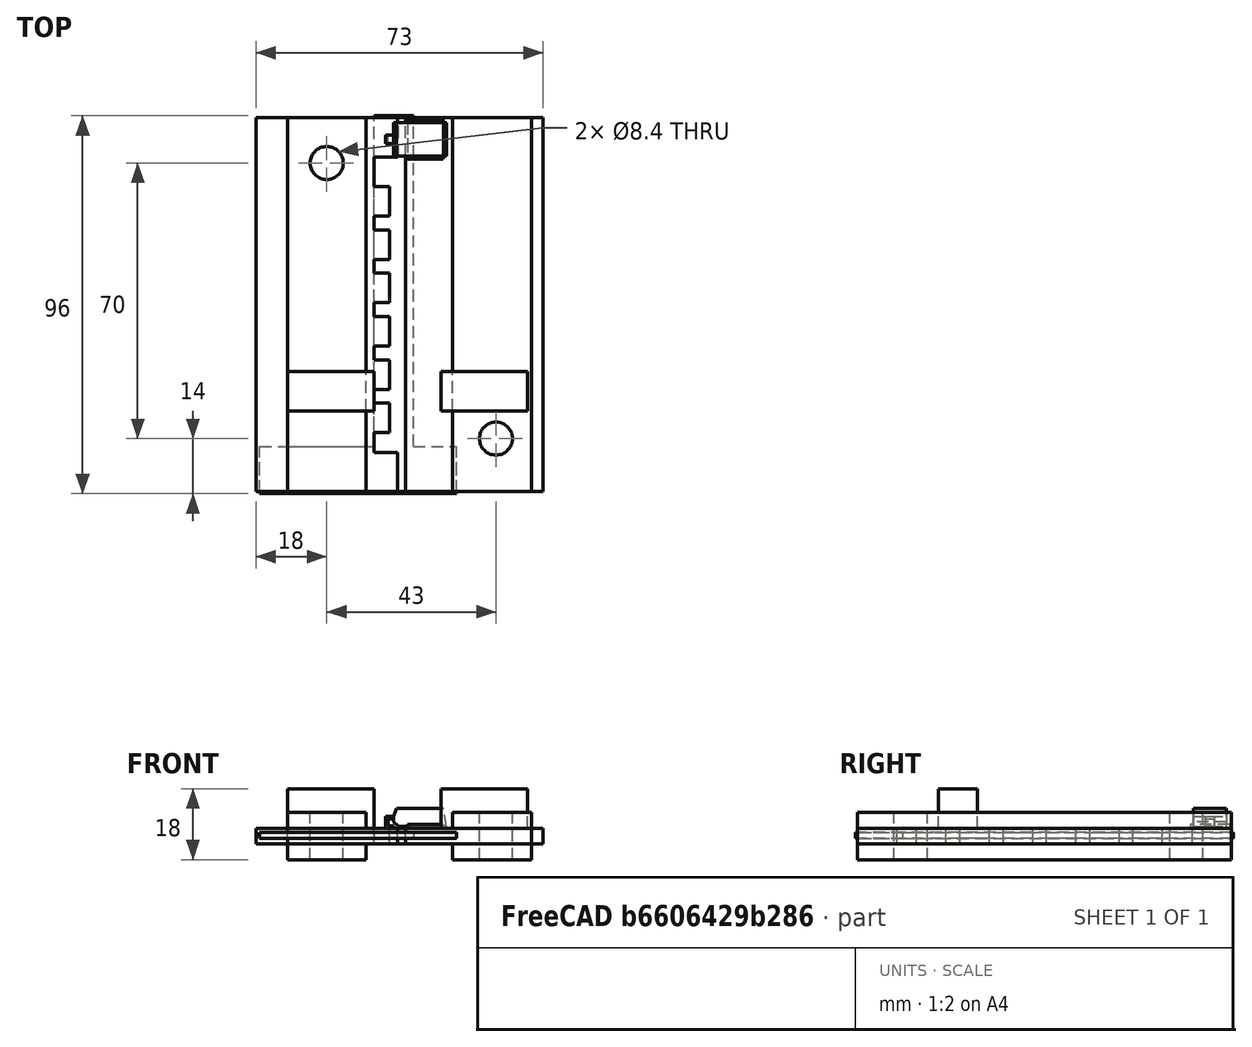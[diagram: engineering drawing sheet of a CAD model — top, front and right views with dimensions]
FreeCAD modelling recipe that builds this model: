
FCSTD DOCUMENT  (FreeCAD 0.17R13541 (Git))
Label: mos3d
License: All rights reserved
LicenseURL: http://en.wikipedia.org/wiki/All_rights_reserved
objects: Part::Box×14, Part::Feature×8, Part::MultiFuse×7, Part::FeaturePython×4, Raytracing::RayFeature×4, Part::Cut×3, Part::Cylinder×2, Raytracing::RayProject×1
note: 38 computed .brp shape members not serialized (recipe doc carries the construction recipe); baked Part::Feature solids carry a one-line shape summary decoded from their .brp

FEATURE [Part::Feature] TO263_7_2
  Placement = pos=(0,0,0) rot=(0,0,-1;1.5708rad)
  shape: bbox 33.79 x 17.72 x 8.468 mm, 285 faces, 0 solids (baked)
FEATURE [Part::FeaturePython] Array  # Draft array (typed FeaturePython)
  Angle = 360
  ArrayType = 0
  Axis = (0,0,1)
  Base = -> TO263_7_2
  Center = (0,0,0)
  Fuse = false
  IntervalAxis = (0,0,0)
  IntervalX = (1,0,0)
  IntervalY = (0,11,0)
  IntervalZ = (0,0,0)
  NumberPolar = 1
  NumberX = 1
  NumberY = 6
  NumberZ = 1
  Placement = pos=(-2,-8,0) rot=(0,0,1;0rad)
FEATURE [Part::Feature] TO263_7_003
  Placement = pos=(0,0,0) rot=(0,0,-1;1.5708rad)
  shape: bbox 33.79 x 17.72 x 8.468 mm, 285 faces, 0 solids (baked)
FEATURE [Part::FeaturePython] Array001  # Draft array (typed FeaturePython)
  Angle = 360
  ArrayType = 0
  Axis = (0,0,1)
  Base = -> TO263_7_003
  Center = (0,0,0)
  Fuse = false
  IntervalAxis = (0,0,0)
  IntervalX = (1,0,0)
  IntervalY = (0,11,0)
  IntervalZ = (0,0,0)
  NumberPolar = 1
  NumberX = 1
  NumberY = 6
  NumberZ = 1
  Placement = pos=(0,53.52,-4) rot=(1,0,0;3.14159rad)
FEATURE [Part::Box] Box  label="铜板2"
  AttacherType = Attacher::AttachEngine3D
  Height = 4
  Length = 32
  Placement = pos=(-3,-19.5,-4) rot=(0,0,1;0rad)
  Width = 95
FEATURE [Part::Box] Box001  label="立方体001"
  AttacherType = Attacher::AttachEngine3D
  Height = 4
  Length = 4
  Placement = pos=(-11,50.5,-4) rot=(0,0,1;0rad)
  Width = 7.5
FEATURE [Part::FeaturePython] Array002  # Draft array (typed FeaturePython)
  Angle = 360
  ArrayType = 0
  Axis = (0,0,1)
  Base = -> Box001
  Center = (0,0,0)
  Fuse = false
  IntervalAxis = (0,0,0)
  IntervalX = (1,0,0)
  IntervalY = (0,-11,0)
  IntervalZ = (0,0,0)
  NumberPolar = 1
  NumberX = 1
  NumberY = 6
  NumberZ = 1
FEATURE [Part::Box] Box002  label="立方体002"
  AttacherType = Attacher::AttachEngine3D
  Height = 4
  Length = 22
  Placement = pos=(-33,-19.5,-4) rot=(0,0,1;0rad)
  Width = 95
FEATURE [Part::Box] Box003  label="pcb"
  AttacherType = Attacher::AttachEngine3D
  Height = 4
  Length = 40
  Placement = pos=(-25,-19.5,-4) rot=(0,0,1;0rad)
  Width = 95
FEATURE [Part::MultiFuse] Fusion  label="铜板1"
  Shapes = -> [Box002,Array002]
FEATURE [Part::Box] Box004  label="tvs"
  AttacherType = Attacher::AttachEngine3D
  Height = 4
  Length = 6
  Placement = pos=(-11,-19.5,-4) rot=(0,0,1;0rad)
  Width = 10
FEATURE [Part::Box] Box005  label="tvs001"
  AttacherType = Attacher::AttachEngine3D
  Height = 4
  Length = 6
  Placement = pos=(-11,65.5,-4) rot=(0,0,1;0rad)
  Width = 10
FEATURE [Part::MultiFuse] Fusion001  label="铜板003"
  Shapes = -> [Box005,Box004,Fusion]
FEATURE [Part::MultiFuse] Fusion002  label="铜板"
  Shapes = -> [Box,Fusion001]
FEATURE [Raytracing::RayFeature] Cut_View
  Result = <blob: 16373 chars omitted>
  Transparency = 0
FEATURE [Raytracing::RayFeature] Array001_View
  Result = <blob: 3290098 chars omitted>
  Source = -> Array001
  Transparency = 0
FEATURE [Raytracing::RayFeature] Array_View
  Result = <blob: 3232013 chars omitted>
  Source = -> Array
  Transparency = 0
FEATURE [Raytracing::RayFeature] Fusion002_View
  Result = <blob: 25159 chars omitted>
  Source = -> Fusion002
  Transparency = 0
FEATURE [Raytracing::RayProject] PovProject
  Camera = // declares position and view direction\n\n// Generated by FreeCAD (http://www.freecadweb.org/)\n#declare cam_location =  <-82.0449,208.463,-78.9748>;\n#declare cam_look_at  = <11.4052,22.7869,-5.24555>;\n#declare cam_sky      = <0.660922,0.539699,0.521447>;\n#declare cam_angle    = 45; \ncamera {\n  location  cam_location\n  look_at   cam_look_at\n  sky       cam_sky\n  angle     cam_angle \n  right x*2560/1920\n}
  Group = -> [Cut_View,Array001_View,Array_View,Fusion002_View]
  Template = <path>//share/freecad/Mod/Raytracing/Templates/RadiosityOutdoorHQ.pov
FEATURE [Part::Feature] Fusion002001  label="铜板004"
  shape: bbox 73 x 95 x 4 mm, 58 faces, 2 solids (baked)
FEATURE [Part::Cut] Cut
  Base = -> Box003
  Tool = -> Fusion002001
FEATURE [Part::Feature] Fusion002002  label="铜板005"
  shape: bbox 73 x 95 x 4 mm, 58 faces, 2 solids (baked)
FEATURE [Part::Box] Box006  label="立方体"
  AttacherType = Attacher::AttachEngine3D
  Height = 10
  Length = 22
  Placement = pos=(6,1,0) rot=(0,0,1;0rad)
  Width = 10
FEATURE [Part::Box] Box007  label="立方体003"
  AttacherType = Attacher::AttachEngine3D
  Height = 10
  Length = 22
  Placement = pos=(-33,1,0) rot=(0,0,1;0rad)
  Width = 10
FEATURE [Part::Feature] TO263_7_004
  Placement = pos=(0,0,0) rot=(0,0,-1;1.5708rad)
  shape: bbox 33.79 x 17.72 x 8.468 mm, 285 faces, 0 solids (baked)
FEATURE [Part::FeaturePython] Array003  # Draft array (typed FeaturePython)
  Angle = 360
  ArrayType = 0
  Axis = (0,0,1)
  Base = -> TO263_7_004
  Center = (0,0,0)
  Fuse = false
  IntervalAxis = (0,0,0)
  IntervalX = (1,0,0)
  IntervalY = (0,11,0)
  IntervalZ = (0,0,0)
  NumberPolar = 1
  NumberX = 1
  NumberY = 6
  NumberZ = 1
FEATURE [Part::Feature] Part__Feature  label="User Library-DO-218AB"
  Placement = pos=(2,70,0) rot=(0,0.707107,0.707107;3.14159rad)
  shape: bbox 15.43 x 10 x 5 mm, 24 faces, 3 solids (baked)
FEATURE [Part::Feature] Array003001  label="Array004"
  shape: bbox 33.79 x 72.72 x 8.468 mm, 1710 faces, 0 solids (baked)
FEATURE [Part::Feature] Array003002  label="Array005"
  Placement = pos=(0,53.5,-4.6) rot=(1,0,0;3.14159rad)
  shape: bbox 33.79 x 72.72 x 8.468 mm, 1710 faces, 0 solids (baked)
FEATURE [Part::Box] Box008  label="立方体004"
  AttacherType = Attacher::AttachEngine3D
  Height = 1.6
  Length = 10
  Placement = pos=(-11,-19,-2.6) rot=(0,0,1;0rad)
  Width = 95
FEATURE [Part::Box] Box009  label="铜板006"
  AttacherType = Attacher::AttachEngine3D
  Height = 12
  Length = 20
  Placement = pos=(9,-19.5,-8) rot=(0,0,1;0rad)
  Width = 95
FEATURE [Part::Box] Box010  label="铜板007"
  AttacherType = Attacher::AttachEngine3D
  Height = 12
  Length = 20
  Placement = pos=(-33,-19.5,-8) rot=(0,0,1;0rad)
  Width = 95
FEATURE [Part::MultiFuse] Fusion002003
  Shapes = -> [Box010,Box009,Fusion002]
FEATURE [Part::Box] Box011  label="立方体005"
  AttacherType = Attacher::AttachEngine3D
  Height = 1.6
  Length = 50
  Placement = pos=(-40,-20,-2.6) rot=(0,0,1;0rad)
  Width = 12
FEATURE [Part::MultiFuse] Fusion002004  label="pcb001"
  Shapes = -> [Box011,Box008]
FEATURE [Part::Cylinder] Cylinder  label="圆柱体"
  Angle = 360
  AttacherType = Attacher::AttachEngine3D
  Height = 20
  Placement = pos=(20,-6,-10) rot=(0,0,1;0rad)
  Radius = 4.2
FEATURE [Part::Cylinder] Cylinder001  label="圆柱体001"
  Angle = 360
  AttacherType = Attacher::AttachEngine3D
  Height = 20
  Placement = pos=(-23,64,-10) rot=(0,0,1;0rad)
  Radius = 4.2
FEATURE [Part::MultiFuse] Fusion002005
  Shapes = -> [Cylinder001,Cylinder]
FEATURE [Part::Cut] Cut001
  Base = -> Fusion002003
  Tool = -> Fusion002005
FEATURE [Part::Box] Box012  label="立方体006"
  AttacherType = Attacher::AttachEngine3D
  Height = 1.6
  Length = 10
  Placement = pos=(-11,-19,-2.6) rot=(0,0,1;0rad)
  Width = 95
FEATURE [Part::Box] Box013  label="立方体007"
  AttacherType = Attacher::AttachEngine3D
  Height = 1.6
  Length = 50
  Placement = pos=(-40,-20,-2.6) rot=(0,0,1;0rad)
  Width = 12
FEATURE [Part::MultiFuse] Fusion002006
  Shapes = -> [Box013,Box012]
FEATURE [Part::Cut] Cut002  label="紫铜"
  Base = -> Cut001
  Tool = -> Fusion002006
note: 1 file-system path scrubbed to <path> (originals preserved in the JSON sidecar)
